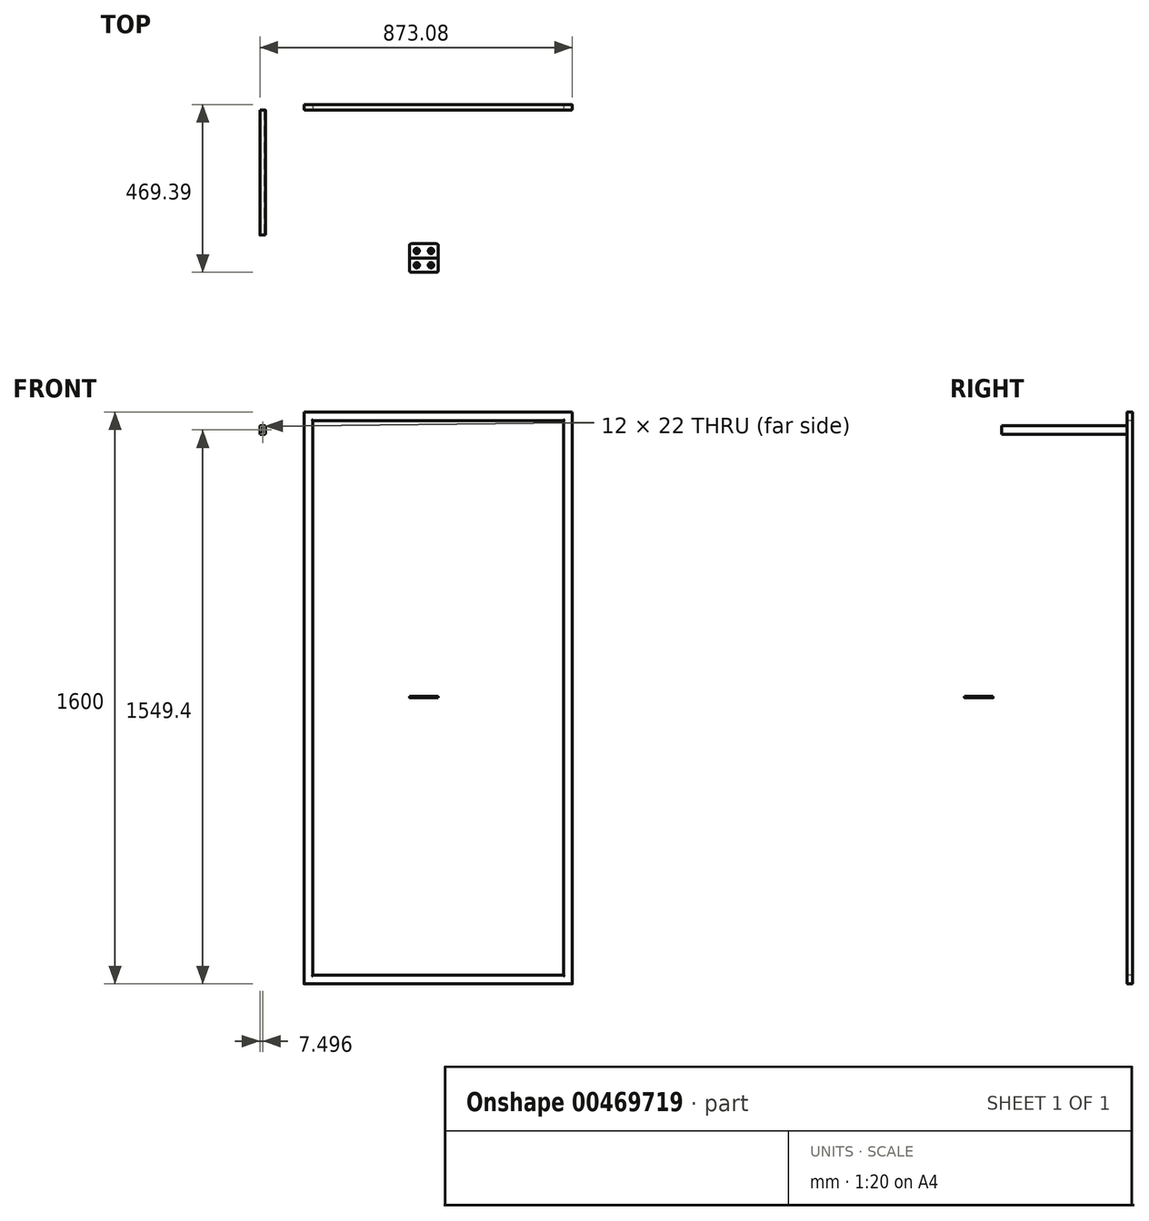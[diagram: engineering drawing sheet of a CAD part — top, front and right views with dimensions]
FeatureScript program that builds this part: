
annotation { "Feature Type Name" : "Feature", "Feature Type Description" : "" }
export const myFeature = defineFeature(function(context is Context, id is Id, definition is map)
    precondition{}
    {
        {
            var Q0;
            Q0=qCreatedBy(makeId("Front.planeOp"),FACE);
            var sketch = newSketch(context, id + "F0", { "sketchPlane" : qUnion([Q0])});
            skLineSegment(sketch, "E0.bottom", {"start": v(-375, 800) * mm, "end": v(375, 800) * mm});
            skLineSegment(sketch, "E0.top", {"start": v(-375, -800) * mm, "end": v(375, -800) * mm});
            skLineSegment(sketch, "E0.left", {"start": v(-375, 800) * mm, "end": v(-375, -800) * mm});
            skLineSegment(sketch, "E0.right", {"start": v(375, 800) * mm, "end": v(375, -800) * mm});
            skLineSegment(sketch, "E1.0", {"start": v(-350, 775) * mm, "end": v(350, 775) * mm});
            skLineSegment(sketch, "E1.1", {"start": v(-350, 775) * mm, "end": v(-350, -775) * mm});
            skLineSegment(sketch, "E1.2", {"start": v(-350, -775) * mm, "end": v(350, -775) * mm});
            skLineSegment(sketch, "E1.3", {"start": v(350, 775) * mm, "end": v(350, -775) * mm});
            skSolve(sketch);
        }
        {
            var Q0;
            Q0=makeQuery(id+"F0.imprint","IMPRINT",FACE,{"disambiguationData":[TD([[makeQuery(id+"F0.imprint","IMPRINT",EDGE,{"derivedFrom":sQuery(id+"F0.wireOp",EDGE,"E0.bottom")}),-1.0]])]});
            extrude(context, id + "F1", {"entities" : qUnion([Q0]), "oppositeDirection" : true, "depth" : 15 * mm});
        }
        {
            var Q0;
            Q0=makeQuery(id+"F1.opExtrude","CAP_FACE",FACE,{"disambiguationData":[OSD([sQuery(id+"F0.wireOp",EDGE,"E0.bottom"),sQuery(id+"F0.wireOp",EDGE,"E0.top"),sQuery(id+"F0.wireOp",EDGE,"E0.left"),sQuery(id+"F0.wireOp",EDGE,"E0.right"),sQuery(id+"F0.wireOp",EDGE,"E1.0"),sQuery(id+"F0.wireOp",EDGE,"E1.1"),sQuery(id+"F0.wireOp",EDGE,"E1.2"),sQuery(id+"F0.wireOp",EDGE,"E1.3")])],"isStart":true});
            var sketch = newSketch(context, id + "F2", { "sketchPlane" : qUnion([Q0])});
            skLineSegment(sketch, "E2.bottom", {"start": v(-498.08, 761.9) * mm, "end": v(-483.08, 761.9) * mm});
            skLineSegment(sketch, "E2.top", {"start": v(-498.08, 736.9) * mm, "end": v(-483.08, 736.9) * mm});
            skLineSegment(sketch, "E2.left", {"start": v(-498.08, 761.9) * mm, "end": v(-498.08, 736.9) * mm});
            skLineSegment(sketch, "E2.right", {"start": v(-483.08, 761.9) * mm, "end": v(-483.08, 736.9) * mm});
            skLineSegment(sketch, "E3.0", {"start": v(-496.58, 760.4) * mm, "end": v(-484.58, 760.4) * mm});
            skLineSegment(sketch, "E3.1", {"start": v(-496.58, 760.4) * mm, "end": v(-496.58, 738.4) * mm});
            skLineSegment(sketch, "E3.2", {"start": v(-496.58, 738.4) * mm, "end": v(-484.58, 738.4) * mm});
            skLineSegment(sketch, "E3.3", {"start": v(-484.58, 760.4) * mm, "end": v(-484.58, 738.4) * mm});
            skSolve(sketch);
        }
        {
            var Q0;
            Q0 = qSketchRegion(id + "F2", true);
            extrude(context, id + "F3", {"entities" : qUnion([Q0]), "depth" : 350 * mm});
        }
        {
            var Q0;
            Q0=qCreatedBy(makeId("Top.planeOp"),FACE);
            var sketch = newSketch(context, id + "F4", { "sketchPlane" : qUnion([Q0])});
            skLineSegment(sketch, "E4.bottom", {"start": v(-75, -374.4) * mm, "end": v(-5, -374.4) * mm});
            skLineSegment(sketch, "E4.top", {"start": v(-80, -414.4) * mm, "end": v(0, -414.4) * mm});
            skLineSegment(sketch, "E4.left", {"start": v(-80, -379.4) * mm, "end": v(-80, -414.4) * mm});
            skLineSegment(sketch, "E4.right", {"start": v(0, -379.4) * mm, "end": v(0, -414.4) * mm});
            skCircle(sketch, "E5", {"center": v(-60, -394.4) * mm, "radius": 2.5 * mm});
            skPoint(sketch, "E5.centerSnap0", {"position": v(-80, -394.4) * mm});
            skCircle(sketch, "E6", {"center": v(-20, -394.4) * mm, "radius": 2.5 * mm});
            skPoint(sketch, "E7.visualSharp", {"position": v(-80, -374.4) * mm});
            skArc(sketch, "E7.filletArc", {"start": v(-75, -374.4) * mm, "mid": v(-78.54, -375.86) * mm, "end": v(-80, -379.4) * mm});
            skPoint(sketch, "E8.visualSharp", {"position": v(0, -374.4) * mm});
            skArc(sketch, "E8.filletArc", {"start": v(0, -379.4) * mm, "mid": v(-1.46, -375.86) * mm, "end": v(-5, -374.4) * mm});
            skSolve(sketch);
        }
        {
            var Q0;
            Q0 = qSketchRegion(id + "F4", true);
            extrude(context, id + "F5", {"entities" : qUnion([Q0]), "depth" : 4 * mm});
        }
        {
            var Q0;
            Q0=makeQuery(id+"F5.opExtrude","CAP_EDGE",EDGE,{"disambiguationData":[OSD([sQuery(id+"F4.wireOp",EDGE,"E6")])],"isStart":false});
            var Q1;
            Q1=makeQuery(id+"F5.opExtrude","CAP_EDGE",EDGE,{"disambiguationData":[OSD([sQuery(id+"F4.wireOp",EDGE,"E5")])],"isStart":false});
            chamfer(context, id + "F6", {"entities" : qUnion([Q0, Q1]), "width" : 5 * mm, "tangentPropagation" : true});
        }
        {
            var Q0;
            Q0=makeQuery(id+"F5.opExtrude","SWEPT_BODY",BODY,{"disambiguationData":[OSD([sQuery(id+"F4.wireOp",EDGE,"E4.bottom"),sQuery(id+"F4.wireOp",EDGE,"E4.top"),sQuery(id+"F4.wireOp",EDGE,"E4.left"),sQuery(id+"F4.wireOp",EDGE,"E4.right"),sQuery(id+"F4.wireOp",EDGE,"E5"),sQuery(id+"F4.wireOp",EDGE,"E6"),sQuery(id+"F4.wireOp",EDGE,"E7.filletArc"),sQuery(id+"F4.wireOp",EDGE,"E8.filletArc")])]});
            var Q1;
            Q1=makeQuery(id+"F5.opExtrude","SWEPT_FACE",FACE,{"disambiguationData":[OSD([sQuery(id+"F4.wireOp",EDGE,"E4.top")])]});
            mirror(context, id + "F7", {"entities" : qUnion([Q0]), "mirrorPlane" : qUnion([Q1])});
        }
        {
            var Q0;
            Q0=makeQuery(id+"F1.opExtrude","CAP_EDGE",EDGE,{"disambiguationData":[OSD([sQuery(id+"F0.wireOp",EDGE,"E1.1")])],"isStart":true});
            var Q1;
            Q1=makeQuery(id+"F1.opExtrude","CAP_EDGE",EDGE,{"disambiguationData":[OSD([sQuery(id+"F0.wireOp",EDGE,"E1.0")])],"isStart":true});
            var Q2;
            Q2=makeQuery(id+"F1.opExtrude","CAP_EDGE",EDGE,{"disambiguationData":[OSD([sQuery(id+"F0.wireOp",EDGE,"E1.3")])],"isStart":true});
            var Q3;
            Q3=makeQuery(id+"F1.opExtrude","CAP_EDGE",EDGE,{"disambiguationData":[OSD([sQuery(id+"F0.wireOp",EDGE,"E1.2")])],"isStart":false});
            var Q4;
            Q4=makeQuery(id+"F1.opExtrude","CAP_EDGE",EDGE,{"disambiguationData":[OSD([sQuery(id+"F0.wireOp",EDGE,"E1.2")])],"isStart":true});
            var Q5;
            Q5=makeQuery(id+"F1.opExtrude","CAP_EDGE",EDGE,{"disambiguationData":[OSD([sQuery(id+"F0.wireOp",EDGE,"E1.1")])],"isStart":false});
            var Q6;
            Q6=makeQuery(id+"F1.opExtrude","CAP_EDGE",EDGE,{"disambiguationData":[OSD([sQuery(id+"F0.wireOp",EDGE,"E1.0")])],"isStart":false});
            var Q7;
            Q7=makeQuery(id+"F3.opExtrude","SWEPT_EDGE",EDGE,{"disambiguationData":[OSD([sQuery(id+"F2.wireOp",EDGE,"E2.top"),sQuery(id+"F2.wireOp",EDGE,"E2.right")])]});
            var Q8;
            Q8=makeQuery(id+"F3.opExtrude","SWEPT_EDGE",EDGE,{"disambiguationData":[OSD([sQuery(id+"F2.wireOp",EDGE,"E2.bottom"),sQuery(id+"F2.wireOp",EDGE,"E2.left")])]});
            var Q9;
            Q9=makeQuery(id+"F3.opExtrude","SWEPT_EDGE",EDGE,{"disambiguationData":[OSD([sQuery(id+"F2.wireOp",EDGE,"E2.bottom"),sQuery(id+"F2.wireOp",EDGE,"E2.right")])]});
            var Q10;
            Q10=makeQuery(id+"F3.opExtrude","SWEPT_EDGE",EDGE,{"disambiguationData":[OSD([sQuery(id+"F2.wireOp",EDGE,"E2.top"),sQuery(id+"F2.wireOp",EDGE,"E2.left")])]});
            fillet(context, id + "F8", {"entities" : qUnion([Q0, Q1, Q2, Q3, Q4, Q5, Q6, Q7, Q8, Q9, Q10]), "radius" : 2.5 * mm, "tangentPropagation" : true, "allowEdgeOverflow" : false});
        }
        {
            var Q0;
            Q0=makeQuery(id+"F1.opExtrude","CAP_EDGE",EDGE,{"disambiguationData":[OSD([sQuery(id+"F0.wireOp",EDGE,"E0.left")])],"isStart":false});
            var Q1;
            Q1=makeQuery(id+"F1.opExtrude","CAP_EDGE",EDGE,{"disambiguationData":[OSD([sQuery(id+"F0.wireOp",EDGE,"E0.left")])],"isStart":true});
            var Q2;
            Q2=makeQuery(id+"F1.opExtrude","CAP_EDGE",EDGE,{"disambiguationData":[OSD([sQuery(id+"F0.wireOp",EDGE,"E0.bottom")])],"isStart":false});
            var Q3;
            Q3=makeQuery(id+"F1.opExtrude","CAP_EDGE",EDGE,{"disambiguationData":[OSD([sQuery(id+"F0.wireOp",EDGE,"E0.bottom")])],"isStart":true});
            var Q4;
            Q4=makeQuery(id+"F1.opExtrude","CAP_EDGE",EDGE,{"disambiguationData":[OSD([sQuery(id+"F0.wireOp",EDGE,"E0.right")])],"isStart":true});
            var Q5;
            Q5=makeQuery(id+"F1.opExtrude","CAP_EDGE",EDGE,{"disambiguationData":[OSD([sQuery(id+"F0.wireOp",EDGE,"E0.right")])],"isStart":false});
            var Q6;
            Q6=makeQuery(id+"F1.opExtrude","CAP_EDGE",EDGE,{"disambiguationData":[OSD([sQuery(id+"F0.wireOp",EDGE,"E0.top")])],"isStart":false});
            var Q7;
            Q7=makeQuery(id+"F1.opExtrude","CAP_EDGE",EDGE,{"disambiguationData":[OSD([sQuery(id+"F0.wireOp",EDGE,"E0.top")])],"isStart":true});
            fillet(context, id + "F9", {"entities" : qUnion([Q0, Q1, Q2, Q3, Q4, Q5, Q6, Q7]), "radius" : 2.5 * mm, "tangentPropagation" : true, "allowEdgeOverflow" : false});
        }
    });
